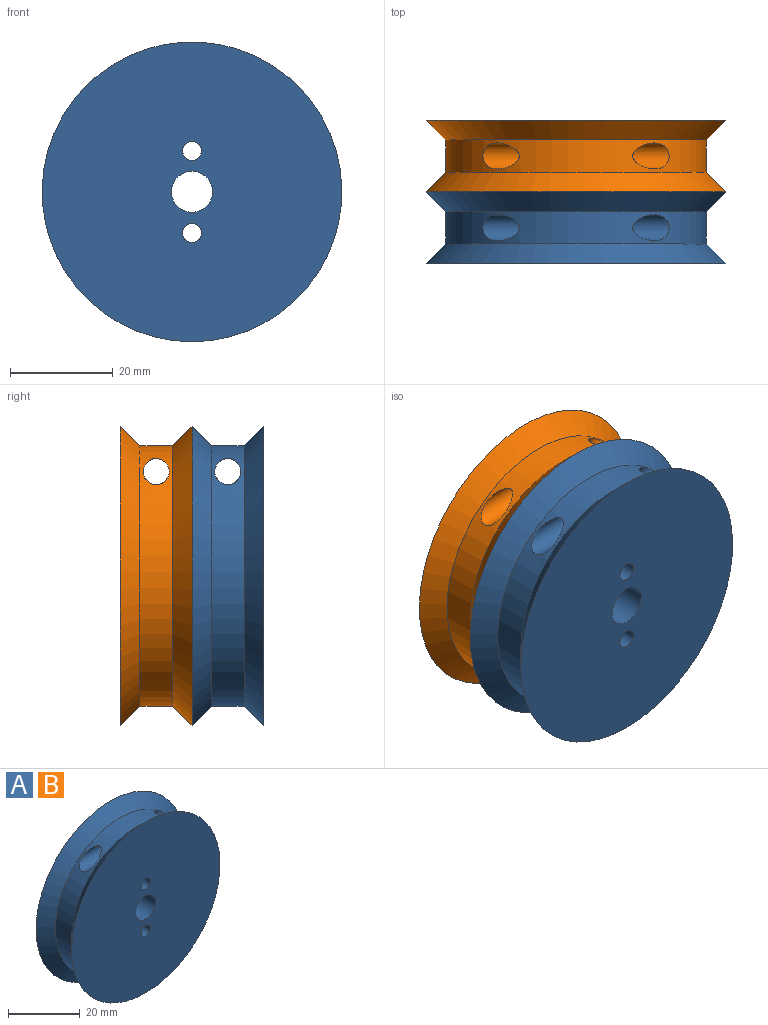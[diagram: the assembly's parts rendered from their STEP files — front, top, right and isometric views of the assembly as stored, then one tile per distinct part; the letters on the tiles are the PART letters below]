
ASSEMBLY  parts=2 mates=1
PART A: 9 faces, bbox 58.4x14x58.4 mm
  f0: cylinder r=25.4mm len=50.8mm, axis (0,1,0), area 944.2mm2, adj f6,f7,f8
  f1: plane 58.42x58.42mm, normal (0,1,0), area 2608.7mm2, adj f3,f4,f5,f8
  f2: plane 58.42x58.42mm, normal (0,-1,0), area 2608.7mm2, adj f3,f4,f5,f7
  f3: cylinder r=1.85mm len=13.97mm, axis (0,-1,0), area 162.4mm2, adj f1,f2
  f4: cylinder r=4mm len=13.97mm, axis (0,-1,0), area 351.1mm2, adj f1,f2
  f5: cylinder r=1.85mm len=13.97mm, axis (0,-1,0), area 162.4mm2, adj f1,f2
  f6: cylinder r=2.54mm len=36.28mm, axis (-1,0,0), area 476.5mm2, adj f0
  f7: cone r=31.75mm half-angle=45deg, axis (0,-1,0), area 924.4mm2, adj f0,f2
  f8: cone r=25.4mm half-angle=45deg, axis (0,1,0), area 924.4mm2, adj f0,f1
PART B: same geometry as A
PLACE A t=(-26.91,-6.93,2.43)mm
PLACE B t=(-26.91,7.04,2.43)mm
MATE fastened B.f5 <-> A.f5  axis (0,-1,0) through (-26.91,-6.93,10.43)mm
